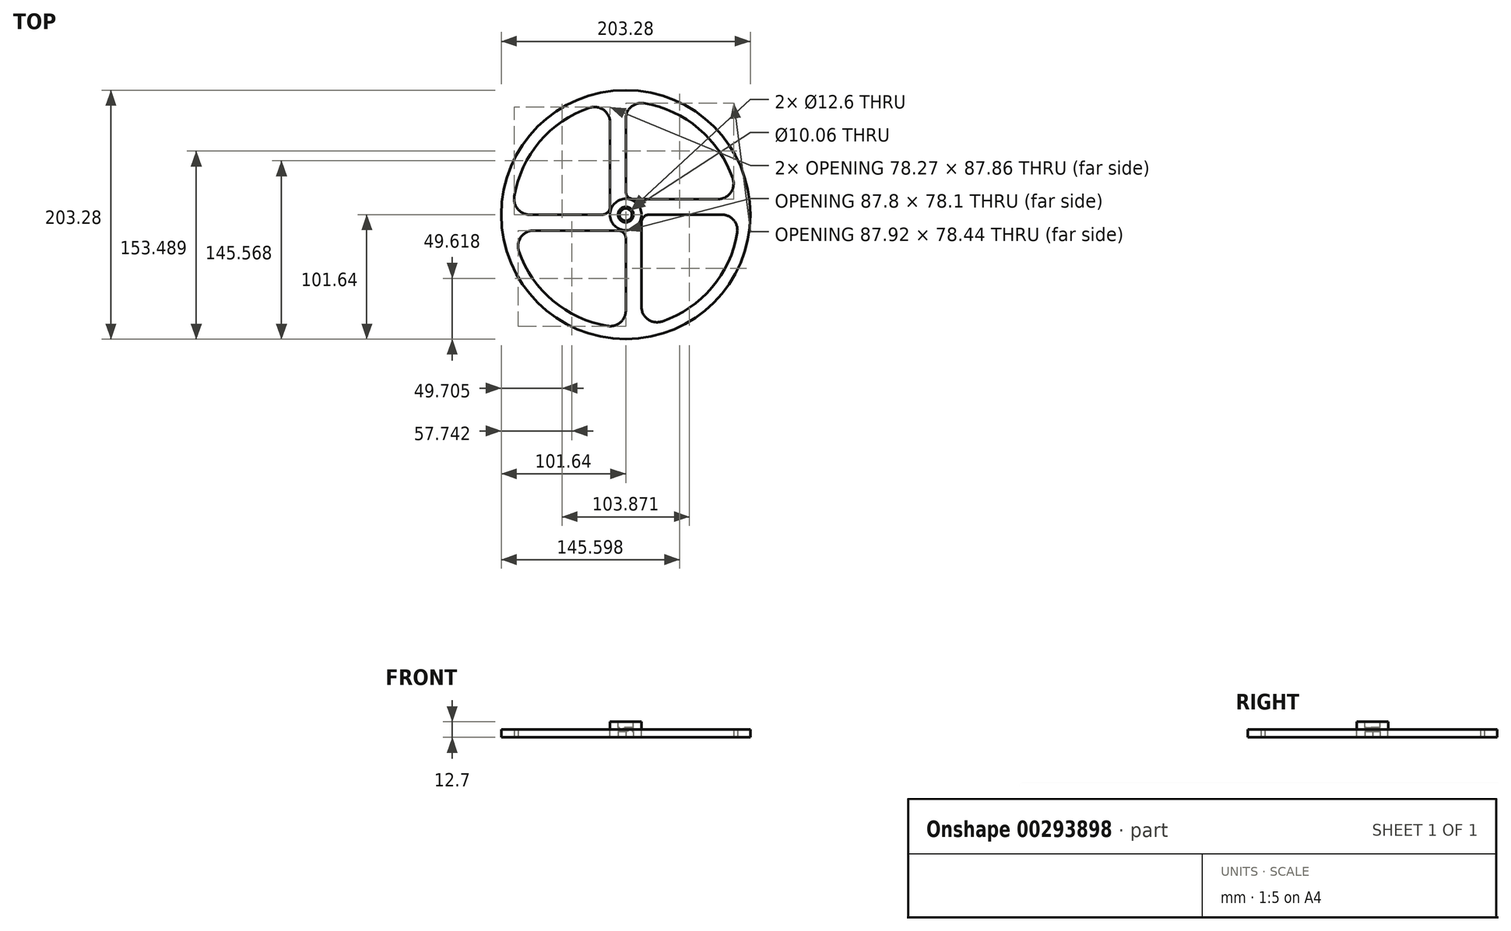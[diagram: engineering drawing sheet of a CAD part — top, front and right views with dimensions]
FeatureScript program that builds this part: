
annotation { "Feature Type Name" : "Feature", "Feature Type Description" : "" }
export const myFeature = defineFeature(function(context is Context, id is Id, definition is map)
    precondition{}
    {
        {
            var Q0;
            Q0=qCreatedBy(makeId("Top.planeOp"),FACE);
            var sketch = newSketch(context, id + "F0", { "sketchPlane" : qUnion([Q0])});
            skCircle(sketch, "E0", {"center": v(0, 0) * mm, "radius": 101.64 * mm});
            skCircle(sketch, "E1", {"center": v(0, 0) * mm, "radius": 92.11 * mm});
            skLineSegment(sketch, "E2.left", {"start": v(0, 0) * mm, "end": v(0, 12.75) * mm});
            skLineSegment(sketch, "E3.bottom", {"start": v(0, 0) * mm, "end": v(12.8, 0) * mm});
            skLineSegment(sketch, "E3.left", {"start": v(0, -19.32) * mm, "end": v(0, -95.3) * mm});
            skLineSegment(sketch, "E3.right", {"start": v(12.8, -6.35) * mm, "end": v(12.8, -95.3) * mm});
            skLineSegment(sketch, "E4.bottom", {"start": v(-19.15, 0) * mm, "end": v(-95.48, 0) * mm});
            skLineSegment(sketch, "E4.top", {"start": v(-6.35, -12.97) * mm, "end": v(-95.48, -12.97) * mm});
            skLineSegment(sketch, "E4.left", {"start": v(0, 0) * mm, "end": v(0, -12.97) * mm});
            skLineSegment(sketch, "E5.bottom", {"start": v(0, 0) * mm, "end": v(-12.8, 0) * mm});
            skLineSegment(sketch, "E5.left", {"start": v(0, 18.98) * mm, "end": v(0, 95.3) * mm});
            skLineSegment(sketch, "E5.right", {"start": v(-12.8, 6.35) * mm, "end": v(-12.8, 95.3) * mm});
            skLineSegment(sketch, "E6.bottom", {"start": v(19.15, 0) * mm, "end": v(96.17, 0) * mm});
            skLineSegment(sketch, "E6.top", {"start": v(6.35, 12.63) * mm, "end": v(96.17, 12.63) * mm});
            skLineSegment(sketch, "E6.left", {"start": v(0, 0) * mm, "end": v(0, 12.63) * mm});
            skArc(sketch, "E7.filletArc", {"start": v(-19.15, 0) * mm, "mid": v(-14.66, 1.86) * mm, "end": v(-12.8, 6.35) * mm});
            skArc(sketch, "E8.filletArc", {"start": v(0, -19.32) * mm, "mid": v(-1.86, -14.83) * mm, "end": v(-6.35, -12.97) * mm});
            skArc(sketch, "E9.filletArc", {"start": v(19.15, 0) * mm, "mid": v(14.66, -1.86) * mm, "end": v(12.8, -6.35) * mm});
            skArc(sketch, "E10.filletArc", {"start": v(0, 18.98) * mm, "mid": v(1.86, 14.49) * mm, "end": v(6.35, 12.63) * mm});
            skPoint(sketch, "E11", {"position": v(-12.8, 91.22) * mm});
            skPoint(sketch, "E12", {"position": v(0, 92.11) * mm});
            skPoint(sketch, "E13", {"position": v(91.24, 12.63) * mm});
            skPoint(sketch, "E14", {"position": v(92.11, 0) * mm});
            skPoint(sketch, "E15", {"position": v(12.8, -91.22) * mm});
            skPoint(sketch, "E16", {"position": v(0, -92.11) * mm});
            skPoint(sketch, "E17", {"position": v(-91.2, -12.97) * mm});
            skPoint(sketch, "E18", {"position": v(-92.11, 0) * mm});
            skSolve(sketch);
        }
        {
            var Q0;
            Q0=makeQuery(id+"F0.imprint","IMPRINT",FACE,{"disambiguationData":[TD([[makeQuery(id+"F0.imprint","IMPRINT",EDGE,{"derivedFrom":sQuery(id+"F0.wireOp",EDGE,"E0")}),1.0]])]});
            var Q1;
            {var subQ4=sQuery(id+"F0.wireOp",EDGE,"E7.filletArc");Q1=makeQuery(id+"F0.imprint","IMPRINT",FACE,{"disambiguationData":[TD([[makeQuery(id+"F0.imprint","IMPRINT",EDGE,{"derivedFrom":subQ4}),-1.0]])]});}
            extrude(context, id + "F1", {"entities" : qUnion([Q0, Q1]), "depth" : 6.35 * mm});
        }
        {
            var Q0;
            Q0=makeQuery(id+"F1.opExtrude","SWEPT_EDGE",EDGE,{"disambiguationData":[OSD([sQuery(id+"F0.wireOp",EDGE,"E1"),sQuery(id+"F0.wireOp",EDGE,"E4.top")])]});
            var Q1;
            Q1=makeQuery(id+"F1.opExtrude","SWEPT_EDGE",EDGE,{"disambiguationData":[OSD([sQuery(id+"F0.wireOp",EDGE,"E1"),sQuery(id+"F0.wireOp",EDGE,"E5.left")])]});
            fillet(context, id + "F2", {"entities" : qUnion([Q0, Q1]), "radius" : 12.7 * mm, "tangentPropagation" : true, "allowEdgeOverflow" : false});
        }
        {
            var Q0;
            Q0=makeQuery(id+"F1.opExtrude","SWEPT_EDGE",EDGE,{"disambiguationData":[OSD([sQuery(id+"F0.wireOp",EDGE,"E1"),sQuery(id+"F0.wireOp",EDGE,"E3.right")])]});
            var Q1;
            Q1=makeQuery(id+"F1.opExtrude","SWEPT_EDGE",EDGE,{"disambiguationData":[OSD([sQuery(id+"F0.wireOp",EDGE,"E1"),sQuery(id+"F0.wireOp",EDGE,"E4.bottom")])]});
            fillet(context, id + "F3", {"entities" : qUnion([Q0, Q1]), "radius" : 12.7 * mm, "tangentPropagation" : true, "allowEdgeOverflow" : false});
        }
        {
            var Q0;
            Q0=makeQuery(id+"F1.opExtrude","SWEPT_EDGE",EDGE,{"disambiguationData":[OSD([sQuery(id+"F0.wireOp",EDGE,"E1"),sQuery(id+"F0.wireOp",EDGE,"E5.right")])]});
            var Q1;
            Q1=makeQuery(id+"F1.opExtrude","SWEPT_EDGE",EDGE,{"disambiguationData":[OSD([sQuery(id+"F0.wireOp",EDGE,"E1"),sQuery(id+"F0.wireOp",EDGE,"E6.bottom")])]});
            fillet(context, id + "F4", {"entities" : qUnion([Q0, Q1]), "radius" : 12.7 * mm, "tangentPropagation" : true, "allowEdgeOverflow" : false});
        }
        {
            var Q0;
            Q0=makeQuery(id+"F1.opExtrude","SWEPT_EDGE",EDGE,{"disambiguationData":[OSD([sQuery(id+"F0.wireOp",EDGE,"E1"),sQuery(id+"F0.wireOp",EDGE,"E6.top")])]});
            var Q1;
            Q1=makeQuery(id+"F1.opExtrude","SWEPT_EDGE",EDGE,{"disambiguationData":[OSD([sQuery(id+"F0.wireOp",EDGE,"E1"),sQuery(id+"F0.wireOp",EDGE,"E3.left")])]});
            fillet(context, id + "F5", {"entities" : qUnion([Q0, Q1]), "radius" : 12.7 * mm, "tangentPropagation" : true, "allowEdgeOverflow" : false});
        }
        {
            var Q0;
            Q0=makeQuery(id+"F1.opExtrude","CAP_FACE",FACE,{"disambiguationData":[OSD([sQuery(id+"F0.wireOp",EDGE,"E0"),sQuery(id+"F0.wireOp",EDGE,"E1"),sQuery(id+"F0.wireOp",EDGE,"E3.left"),sQuery(id+"F0.wireOp",EDGE,"E3.right"),sQuery(id+"F0.wireOp",EDGE,"E4.bottom"),sQuery(id+"F0.wireOp",EDGE,"E4.top"),sQuery(id+"F0.wireOp",EDGE,"E5.left"),sQuery(id+"F0.wireOp",EDGE,"E5.right"),sQuery(id+"F0.wireOp",EDGE,"E6.bottom"),sQuery(id+"F0.wireOp",EDGE,"E6.top"),sQuery(id+"F0.wireOp",EDGE,"E7.filletArc"),sQuery(id+"F0.wireOp",EDGE,"E8.filletArc"),sQuery(id+"F0.wireOp",EDGE,"E9.filletArc"),sQuery(id+"F0.wireOp",EDGE,"E10.filletArc")])],"isStart":false});
            var sketch = newSketch(context, id + "F6", { "sketchPlane" : qUnion([Q0])});
            skCircle(sketch, "E19", {"center": v(0, 0) * mm, "radius": 12.86 * mm});
            skSolve(sketch);
        }
        {
            var Q0;
            Q0 = qSketchRegion(id + "F6", true);
            extrude(context, id + "F7", {"entities" : qUnion([Q0]), "operationType" : NewBodyOperationType.ADD, "depth" : 6.35 * mm});
        }
        {
            var Q0;
            Q0=makeQuery(id+"F7.opExtrude","CAP_FACE",FACE,{"disambiguationData":[OSD([sQuery(id+"F6.wireOp",EDGE,"E19")])],"isStart":false});
            var sketch = newSketch(context, id + "F8", { "sketchPlane" : qUnion([Q0])});
            skPoint(sketch, "E20", {"position": v(0, 0) * mm});
            skSolve(sketch);
        }
        {
            var Q0;
            Q0=sQuery(id+"F8.wireOp",VERTEX,"E20");
            var Q1;
            Q1=makeQuery(id+"F1.opExtrude","SWEPT_BODY",BODY,{"disambiguationData":[OSD([sQuery(id+"F0.wireOp",EDGE,"E0"),sQuery(id+"F0.wireOp",EDGE,"E1"),sQuery(id+"F0.wireOp",EDGE,"E3.left"),sQuery(id+"F0.wireOp",EDGE,"E3.right"),sQuery(id+"F0.wireOp",EDGE,"E4.bottom"),sQuery(id+"F0.wireOp",EDGE,"E4.top"),sQuery(id+"F0.wireOp",EDGE,"E5.left"),sQuery(id+"F0.wireOp",EDGE,"E5.right"),sQuery(id+"F0.wireOp",EDGE,"E6.bottom"),sQuery(id+"F0.wireOp",EDGE,"E6.top"),sQuery(id+"F0.wireOp",EDGE,"E7.filletArc"),sQuery(id+"F0.wireOp",EDGE,"E8.filletArc"),sQuery(id+"F0.wireOp",EDGE,"E9.filletArc"),sQuery(id+"F0.wireOp",EDGE,"E10.filletArc")])]});
            hole(context, id + "F9", {"style" : HoleStyle.SIMPLE, "endStyle" : HoleEndStyle.BLIND, "holeDiameter" : 12.6 * mm, "holeDepth" : 4.75 * mm, "tappedDepth" : 12.7 * mm, "tapClearance" : 3, "locations" : qUnion([Q0]), "scope" : qUnion([Q1])});
        }
        {
            var Q0;
            Q0=makeQuery(id+"F1.opExtrude","CAP_FACE",FACE,{"disambiguationData":[OSD([sQuery(id+"F0.wireOp",EDGE,"E0"),sQuery(id+"F0.wireOp",EDGE,"E1"),sQuery(id+"F0.wireOp",EDGE,"E3.left"),sQuery(id+"F0.wireOp",EDGE,"E3.right"),sQuery(id+"F0.wireOp",EDGE,"E4.bottom"),sQuery(id+"F0.wireOp",EDGE,"E4.top"),sQuery(id+"F0.wireOp",EDGE,"E5.left"),sQuery(id+"F0.wireOp",EDGE,"E5.right"),sQuery(id+"F0.wireOp",EDGE,"E6.bottom"),sQuery(id+"F0.wireOp",EDGE,"E6.top"),sQuery(id+"F0.wireOp",EDGE,"E7.filletArc"),sQuery(id+"F0.wireOp",EDGE,"E8.filletArc"),sQuery(id+"F0.wireOp",EDGE,"E9.filletArc"),sQuery(id+"F0.wireOp",EDGE,"E10.filletArc")])],"isStart":true});
            var sketch = newSketch(context, id + "F10", { "sketchPlane" : qUnion([Q0])});
            skPoint(sketch, "E21", {"position": v(0, 0) * mm});
            skSolve(sketch);
        }
        {
            var Q0;
            Q0=sQuery(id+"F10.wireOp",VERTEX,"E21");
            var Q1;
            Q1=makeQuery(id+"F1.opExtrude","SWEPT_BODY",BODY,{"disambiguationData":[OSD([sQuery(id+"F0.wireOp",EDGE,"E0"),sQuery(id+"F0.wireOp",EDGE,"E1"),sQuery(id+"F0.wireOp",EDGE,"E3.left"),sQuery(id+"F0.wireOp",EDGE,"E3.right"),sQuery(id+"F0.wireOp",EDGE,"E4.bottom"),sQuery(id+"F0.wireOp",EDGE,"E4.top"),sQuery(id+"F0.wireOp",EDGE,"E5.left"),sQuery(id+"F0.wireOp",EDGE,"E5.right"),sQuery(id+"F0.wireOp",EDGE,"E6.bottom"),sQuery(id+"F0.wireOp",EDGE,"E6.top"),sQuery(id+"F0.wireOp",EDGE,"E7.filletArc"),sQuery(id+"F0.wireOp",EDGE,"E8.filletArc"),sQuery(id+"F0.wireOp",EDGE,"E9.filletArc"),sQuery(id+"F0.wireOp",EDGE,"E10.filletArc")])]});
            hole(context, id + "F11", {"style" : HoleStyle.SIMPLE, "endStyle" : HoleEndStyle.BLIND, "holeDiameter" : 12.6 * mm, "holeDepth" : 4.75 * mm, "tappedDepth" : 12.7 * mm, "tapClearance" : 3, "locations" : qUnion([Q0]), "scope" : qUnion([Q1])});
        }
        {
            var Q0;
            Q0=sQuery(id+"F10.wireOp",VERTEX,"E21");
            var Q1;
            Q1=makeQuery(id+"F1.opExtrude","SWEPT_BODY",BODY,{"disambiguationData":[OSD([sQuery(id+"F0.wireOp",EDGE,"E0"),sQuery(id+"F0.wireOp",EDGE,"E1"),sQuery(id+"F0.wireOp",EDGE,"E3.left"),sQuery(id+"F0.wireOp",EDGE,"E3.right"),sQuery(id+"F0.wireOp",EDGE,"E4.bottom"),sQuery(id+"F0.wireOp",EDGE,"E4.top"),sQuery(id+"F0.wireOp",EDGE,"E5.left"),sQuery(id+"F0.wireOp",EDGE,"E5.right"),sQuery(id+"F0.wireOp",EDGE,"E6.bottom"),sQuery(id+"F0.wireOp",EDGE,"E6.top"),sQuery(id+"F0.wireOp",EDGE,"E7.filletArc"),sQuery(id+"F0.wireOp",EDGE,"E8.filletArc"),sQuery(id+"F0.wireOp",EDGE,"E9.filletArc"),sQuery(id+"F0.wireOp",EDGE,"E10.filletArc")])]});
            hole(context, id + "F12", {"style" : HoleStyle.SIMPLE, "endStyle" : HoleEndStyle.THROUGH, "holeDiameter" : 10.06 * mm, "tappedDepth" : 12.7 * mm, "tapClearance" : 3, "locations" : qUnion([Q0]), "scope" : qUnion([Q1])});
        }
    });
